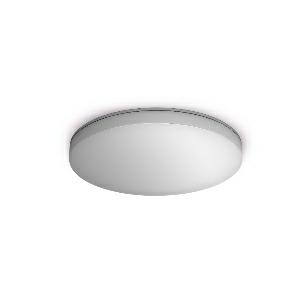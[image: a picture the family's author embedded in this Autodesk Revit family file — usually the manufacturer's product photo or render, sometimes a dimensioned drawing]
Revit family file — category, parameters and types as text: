
# Revit family: rs_pro_connect_r10_sl_057060
name_source: partatom
category: Leuchten
revit_build: Autodesk Revit 2016 (Build: 20190508_0715(x64)
units: mm (PartAtom-declared; Revit-internal decimal feet)

## family parameters
Basisbauteil = Fläche
Beim Laden mit Abzugskörper schneiden = Nein
Bemaßung runder Anschluss = Durchmesser verwenden
Gemeinsam genutzt = Nein
Lichtquelle = Nein
Raumberechnungspunkt = Nein
Teiletyp = Normal

## types (1)
- RS PRO Connect R10 SL (1 x , 1100 lm, 3000 K)
    Beschreibung = Dimensions (Ø x H): 300 x 55 mm; Mains power supply: 220 – 240 V / 50 – 60 Hz; Output: 9 W; Luminous flux: 1100 lm; Colour temperature: 3000 K; Colour variation LED: SDCM3; Colour Rendering Index CRI: 80-89; With lamp: Yes, STEINEL LED system; Lamp: LED cannot be replaced; LED life expectancy (max. °C): 55000 h; LED life expectancy (25 °C): 60000 h; Drop in luminous flux in accordance with LM80: L80B50; Base: without; LED cooling system: Passive Thermo Control; With motion detector: No; Main light adjustable: 50 - 100 %; Continuous light: selectable; Photo-cell controller: No; Basic light level function, detail: LED Backlight; Functions: Backlight; Soft light start: No; Impact resistance: IK07; IP-rating: IP40; Protection class: II; Ambient temperature: -20 – 40 °C; Housing material: Plastic; Cover material: PC, opal; Manufacturer's Warranty: 5 years; Settings via: Bluetooth; With remote control: No; Version: warm white; PU1, EAN: 4007841057060
    CIE Flux Codes = 44 75 93 94 100
    Color Rendering = 80-89
    Color Temperature = 3000 K
    Frequency = 50 Hz, 60 Hz
    Height = 0 mm  [stored 0 ft]
    Hersteller = Steinel
    Lamp Light Flux = 1100 lm
    Lamp count = 1
    Lampe = 1 x
    Length = 300 mm
    Luminous efficacy = 0 lm/W
    ModVariant = Nein
    Modell = 057060
    Mounting Type = Surface mounted
    Number of Poles = 1
    OnlyDefault = Ja
    Power Factor = 1
    Product Name = RS PRO Connect R10 SL
    Product group = Sensor-switched indoor light
    ProductGroupID = 30
    Protection Class = Protection class II
    Protection Degree = IP 40
    RlxData = <blob elided: 167125 chars, md5=5e4a1fc1>
    Scheinlast = 0 VA
    Socket = socket
    Standby Power = 0 W
    System Light Flux = 0 lm
    System Power = 0 W
    Typenbild = produkt1_057060.jpg
    Typenkommentare = Product without accessories
    URL = http://relux.com
    VarID = ---
    Voltage = 0 V
    Vorgabe-Ansicht = 1800 mm
    Weight = 0.00 kg
    Width = 0 mm  [stored 0 ft]

note: [stored X ft] marks values corroborated as IEEE doubles in the binary element streams (Revit-internal decimal feet)

## geometry (parser evidence)
native form markers: Blend x4, Sweep x12
no freeform markers — native parametric forms only
